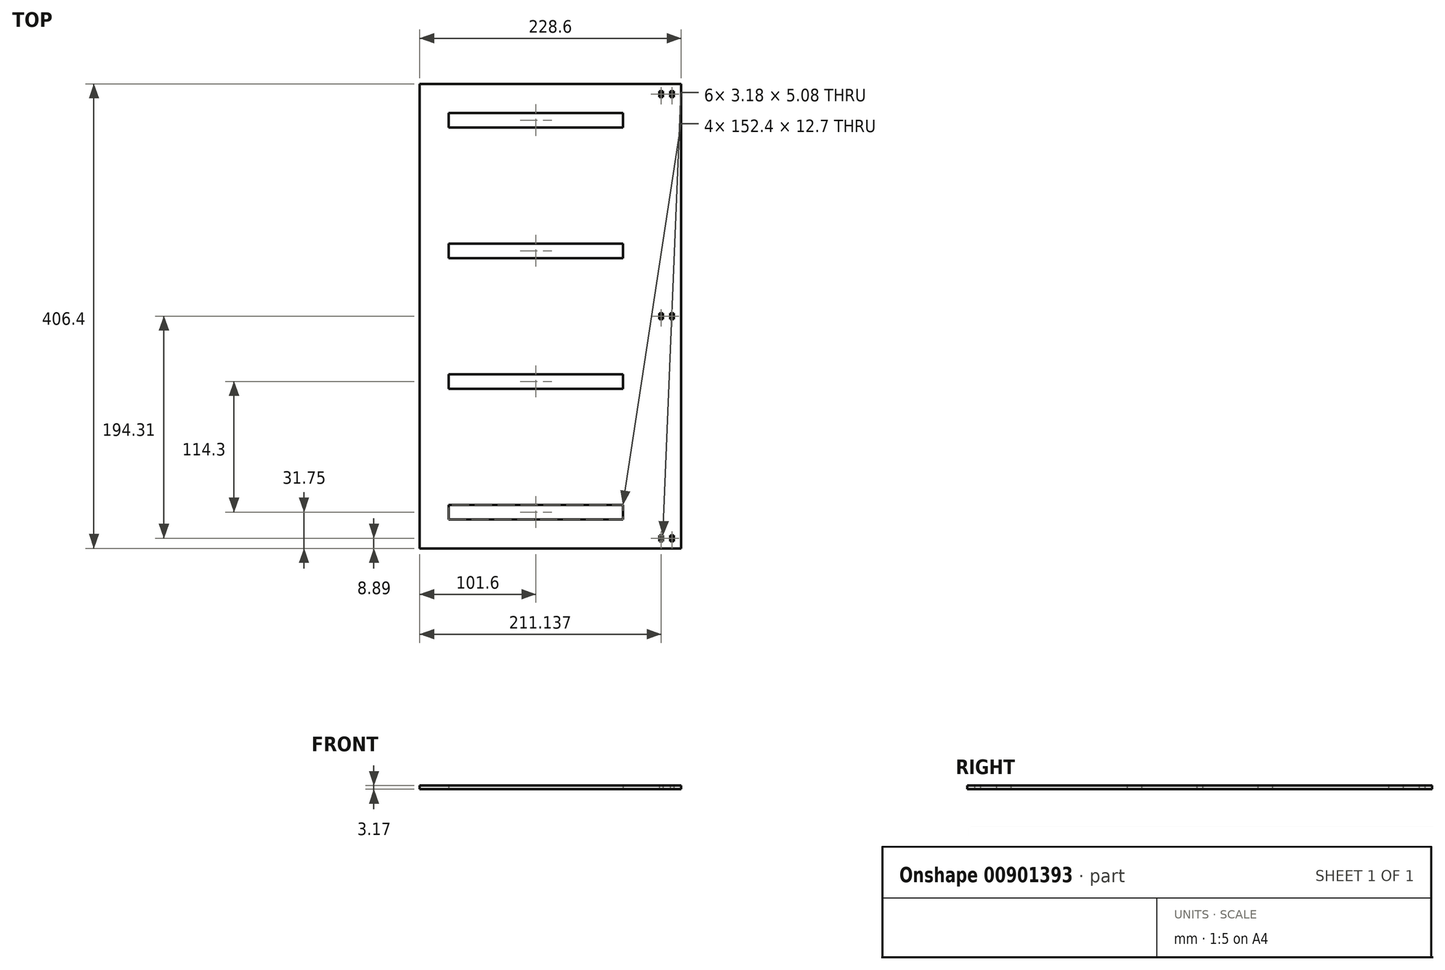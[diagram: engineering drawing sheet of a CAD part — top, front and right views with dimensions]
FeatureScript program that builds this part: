
annotation { "Feature Type Name" : "Feature", "Feature Type Description" : "" }
export const myFeature = defineFeature(function(context is Context, id is Id, definition is map)
    precondition{}
    {
        {
            var Q0;
            Q0=qCreatedBy(makeId("Top.planeOp"),FACE);
            var sketch = newSketch(context, id + "F0", { "sketchPlane" : qUnion([Q0])});
            skLineSegment(sketch, "E0.bottom", {"start": v(0, 0) * mm, "end": v(-228.6, 0) * mm});
            skLineSegment(sketch, "E0.top", {"start": v(0, 406.4) * mm, "end": v(-228.6, 406.4) * mm});
            skLineSegment(sketch, "E0.left", {"start": v(0, 0) * mm, "end": v(0, 406.4) * mm});
            skLineSegment(sketch, "E0.right", {"start": v(-228.6, 0) * mm, "end": v(-228.6, 406.4) * mm});
            skLineSegment(sketch, "E1.bottom", {"start": v(-203.2, 381) * mm, "end": v(-50.8, 381) * mm});
            skLineSegment(sketch, "E1.top", {"start": v(-203.2, 368.3) * mm, "end": v(-50.8, 368.3) * mm});
            skLineSegment(sketch, "E1.left", {"start": v(-203.2, 381) * mm, "end": v(-203.2, 368.3) * mm});
            skLineSegment(sketch, "E1.right", {"start": v(-50.8, 381) * mm, "end": v(-50.8, 368.3) * mm});
            skLineSegment(sketch, "E2", {"start": v(-25.4, 406.4) * mm, "end": v(-25.4, 0) * mm, "construction": true});
            skLineSegment(sketch, "E3.0.1.0", {"start": v(-50.8, 266.7) * mm, "end": v(-50.8, 254) * mm});
            skLineSegment(sketch, "E3.0.1.1", {"start": v(-203.2, 266.7) * mm, "end": v(-50.8, 266.7) * mm});
            skLineSegment(sketch, "E3.0.1.2", {"start": v(-203.2, 254) * mm, "end": v(-50.8, 254) * mm});
            skLineSegment(sketch, "E3.0.1.3", {"start": v(-203.2, 266.7) * mm, "end": v(-203.2, 254) * mm});
            skLineSegment(sketch, "E3.0.2.0", {"start": v(-50.8, 152.4) * mm, "end": v(-50.8, 139.7) * mm});
            skLineSegment(sketch, "E3.0.2.1", {"start": v(-203.2, 152.4) * mm, "end": v(-50.8, 152.4) * mm});
            skLineSegment(sketch, "E3.0.2.2", {"start": v(-203.2, 139.7) * mm, "end": v(-50.8, 139.7) * mm});
            skLineSegment(sketch, "E3.0.2.3", {"start": v(-203.2, 152.4) * mm, "end": v(-203.2, 139.7) * mm});
            skLineSegment(sketch, "E3.direction1", {"start": v(-50.8, 368.3) * mm, "end": v(-25.4, 368.3) * mm, "construction": true});
            skLineSegment(sketch, "E3.direction2", {"start": v(-50.8, 368.3) * mm, "end": v(-50.8, 254) * mm, "construction": true});
            skLineSegment(sketch, "E4.bottom", {"start": v(-19.05, 6.35) * mm, "end": v(-15.88, 6.35) * mm});
            skLineSegment(sketch, "E4.top", {"start": v(-19.05, 11.43) * mm, "end": v(-15.88, 11.43) * mm});
            skLineSegment(sketch, "E4.left", {"start": v(-19.05, 6.35) * mm, "end": v(-19.05, 11.43) * mm});
            skLineSegment(sketch, "E4.right", {"start": v(-15.88, 6.35) * mm, "end": v(-15.88, 11.43) * mm});
            skLineSegment(sketch, "E5.bottom", {"start": v(-9.53, 6.35) * mm, "end": v(-6.35, 6.35) * mm});
            skLineSegment(sketch, "E5.top", {"start": v(-9.53, 11.43) * mm, "end": v(-6.35, 11.43) * mm});
            skLineSegment(sketch, "E5.left", {"start": v(-9.53, 6.35) * mm, "end": v(-9.53, 11.43) * mm});
            skLineSegment(sketch, "E5.right", {"start": v(-6.35, 6.35) * mm, "end": v(-6.35, 11.43) * mm});
            skLineSegment(sketch, "E6.0.1.0", {"start": v(-19.05, 205.74) * mm, "end": v(-15.88, 205.74) * mm});
            skLineSegment(sketch, "E6.0.1.1", {"start": v(-19.05, 200.66) * mm, "end": v(-19.05, 205.74) * mm});
            skLineSegment(sketch, "E6.0.1.2", {"start": v(-9.53, 205.74) * mm, "end": v(-6.35, 205.74) * mm});
            skLineSegment(sketch, "E6.0.1.3", {"start": v(-9.53, 200.66) * mm, "end": v(-6.35, 200.66) * mm});
            skLineSegment(sketch, "E6.0.1.4", {"start": v(-6.35, 200.66) * mm, "end": v(-6.35, 205.74) * mm});
            skLineSegment(sketch, "E6.0.1.5", {"start": v(-15.88, 200.66) * mm, "end": v(-15.88, 205.74) * mm});
            skLineSegment(sketch, "E6.0.1.6", {"start": v(-19.05, 200.66) * mm, "end": v(-15.88, 200.66) * mm});
            skLineSegment(sketch, "E6.0.1.7", {"start": v(-9.53, 200.66) * mm, "end": v(-9.53, 205.74) * mm});
            skLineSegment(sketch, "E6.0.2.0", {"start": v(-19.05, 400.05) * mm, "end": v(-15.88, 400.05) * mm});
            skLineSegment(sketch, "E6.0.2.1", {"start": v(-19.05, 394.97) * mm, "end": v(-19.05, 400.05) * mm});
            skLineSegment(sketch, "E6.0.2.2", {"start": v(-9.53, 400.05) * mm, "end": v(-6.35, 400.05) * mm});
            skLineSegment(sketch, "E6.0.2.3", {"start": v(-9.53, 394.97) * mm, "end": v(-6.35, 394.97) * mm});
            skLineSegment(sketch, "E6.0.2.4", {"start": v(-6.35, 394.97) * mm, "end": v(-6.35, 400.05) * mm});
            skLineSegment(sketch, "E6.0.2.5", {"start": v(-15.88, 394.97) * mm, "end": v(-15.88, 400.05) * mm});
            skLineSegment(sketch, "E6.0.2.6", {"start": v(-19.05, 394.97) * mm, "end": v(-15.88, 394.97) * mm});
            skLineSegment(sketch, "E6.0.2.7", {"start": v(-9.53, 394.97) * mm, "end": v(-9.53, 400.05) * mm});
            skLineSegment(sketch, "E6.direction1", {"start": v(-19.05, 6.35) * mm, "end": v(6.35, 6.35) * mm, "construction": true});
            skLineSegment(sketch, "E6.direction2", {"start": v(-19.05, 6.35) * mm, "end": v(-19.05, 200.66) * mm, "construction": true});
            skLineSegment(sketch, "E7", {"start": v(-19.05, 11.43) * mm, "end": v(-25.4, 11.43) * mm, "construction": true});
            skLineSegment(sketch, "E8", {"start": v(-6.35, 11.43) * mm, "end": v(0, 11.43) * mm, "construction": true});
            skLineSegment(sketch, "E9.0.0.3", {"start": v(-50.8, 38.1) * mm, "end": v(-50.8, 25.4) * mm});
            skLineSegment(sketch, "E9.3.0.3", {"start": v(-203.2, 38.1) * mm, "end": v(-50.8, 38.1) * mm});
            skLineSegment(sketch, "E9.6.0.3", {"start": v(-203.2, 25.4) * mm, "end": v(-50.8, 25.4) * mm});
            skLineSegment(sketch, "E9.9.0.3", {"start": v(-203.2, 38.1) * mm, "end": v(-203.2, 25.4) * mm});
            skSolve(sketch);
        }
        {
            var Q0;
            Q0=makeQuery(id+"F0.imprint","IMPRINT",FACE,{"disambiguationData":[TD([[makeQuery(id+"F0.imprint","IMPRINT",EDGE,{"derivedFrom":sQuery(id+"F0.wireOp",EDGE,"E0.bottom")}),-1.0]])]});
            extrude(context, id + "F1", {"entities" : qUnion([Q0]), "depth" : 3.17 * mm, "offsetDistance" : 25.4 * mm});
        }
    });
